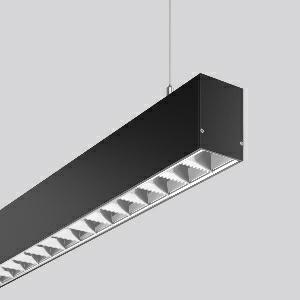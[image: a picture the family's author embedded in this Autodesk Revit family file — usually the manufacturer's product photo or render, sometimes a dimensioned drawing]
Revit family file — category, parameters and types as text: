
# Revit family: less_is_more_50_312338_003_1_76_bd1e
name_source: partatom
category: Lighting Fixtures
units: mm (PartAtom-declared; Revit-internal decimal feet)

## family parameters
Cut with Voids When Loaded = No
Host = Face
Light Source = No
Part Type = Normal
Room Calculation Point = No
Round Connector Dimension = Use Diameter
Shared = No

## types (1)
- LESS IS MORE 50 (1 x LED Modul 840, 5300 lm, 4000)
    Apparent Load = 41 VA
    CIE Flux Codes = 95 100 100 100 100
    Color Rendering = 80
    Color Temperature = 4000
    Default Elevation = 1800 mm
    Description = Series: LESS IS MORE 50
Linear pendant luminaire for aesthetically sophisticated lighting. Housing: extruded aluminium profile, powder-coated. End cap aluminium powder-coated. Canopy made of aluminium, powder-coated. Alea optical system: Reflector structure (ABS, Aluminium-coated, highly polished) with integrated diffuser made of non-yellowing plastic (PMMA) opal for glare-free light at the workstation (screen-compliant according to EN 12464-1). Direct light emission. Suitable for pendant. 2-point steel cable suspension freely positionable and infinitely height-adjustable. Special lengths available on request. LED unit with integrated converter interchangeable and removable. Suitable for through-wiring. With sensors or as a safety luminaire on request. 
Colour: deep black, matt (RAL 9005)
Length: 1687 mm
Width: 57 mm
Height: 75 mm
Suspension length: 2000 mm
Lamp: LED
Socket: without socket
Colour temperature: 4000K
Colour rendering index (CRI): 80
System power: 41 W
Rated luminous flux: 5300 lm
Luminous efficiency: 129 lm/W
Control gear: Converter, dimmable, DALI
Protection class: I
Type of protection: IP 20
    Height = 75 mm
    Lamp = 1 x LED Modul 840
    Lamp Light Flux = 5300 lm
    Lamp count = 1
    Length = 1687 mm
    Lifetime = 50000 h
    Luminous efficacy = 129 lm/W
    Manufacturer = RZB
    ModVariant = No
    Model = 312338.003.1.76
    Mounting Place = Ceiling
    Mounting Type = Pendant
    Number of Poles = 1
    OnlyDefault = Yes
    Power Factor = 1
    Product Name = LESS IS MORE 50
    Product group = Pendant LED linear luminaires
    ProductGroupID = 907
    Protection Class = Protection class I
    Protection Degree = IP 20
    RLX_Detail_Level = 1
    RLX_Emergency_Light_Flux = 0 lm
    RLX_Emergency_Type = 0
    RLX_Emergency_Type_DB = No
    RlxData = <blob elided: 39541 chars, md5=0e858be6>
    Socket = socket
    Standby Power = 0 W
    System Light Flux = 5300 lm
    System Power = 41 W
    Type Comments = Product without accessories
    Type Image = 312342.003.jpg
    URL = http://relux.com
    VarID = ---
    Voltage = 230 V
    Voltage Range = 220-240 V
    Weight = 0.00 kg
    Width = 57 mm

## geometry (parser evidence)
native form markers: Blend x4, Sweep x11
no freeform markers — native parametric forms only
